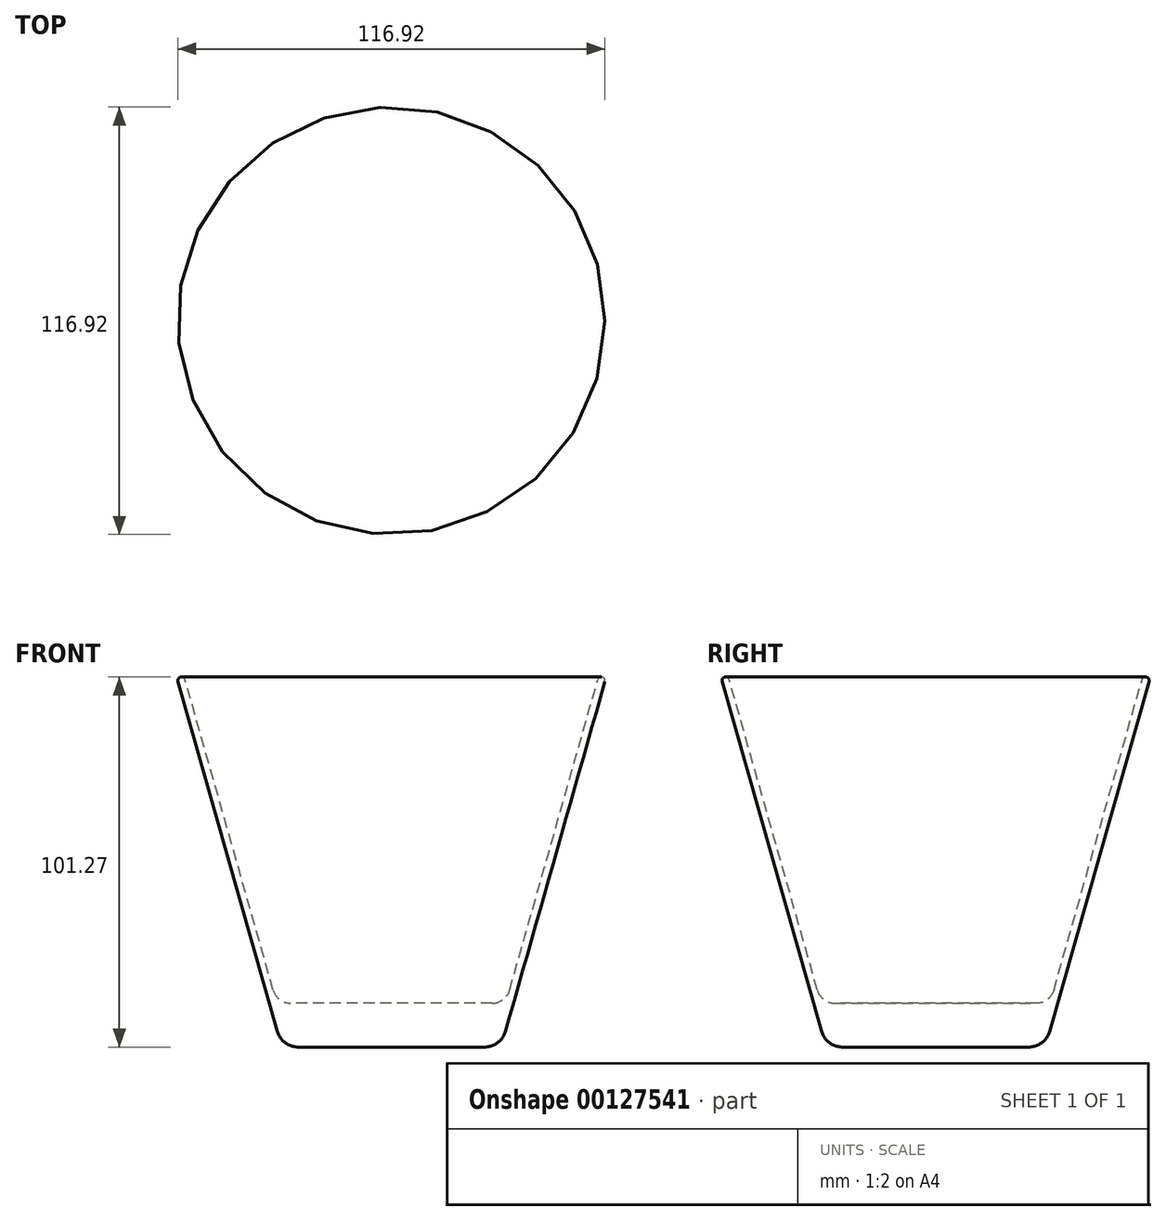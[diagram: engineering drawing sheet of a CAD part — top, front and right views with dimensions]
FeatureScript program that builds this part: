
annotation { "Feature Type Name" : "Feature", "Feature Type Description" : "" }
export const myFeature = defineFeature(function(context is Context, id is Id, definition is map)
    precondition{}
    {
        {
            var Q0;
            Q0=qCreatedBy(makeId("Front.planeOp"),FACE);
            var sketch = newSketch(context, id + "F0", { "sketchPlane" : qUnion([Q0])});
            skLineSegment(sketch, "E0", {"start": v(0, 0) * mm, "end": v(25.47, 0) * mm});
            skLineSegment(sketch, "E1", {"start": v(31.24, 4.36) * mm, "end": v(58.42, 100) * mm});
            skPoint(sketch, "E2.visualSharp", {"position": v(30, 0) * mm});
            skLineSegment(sketch, "E3.0", {"start": v(32.36, 15.63) * mm, "end": v(56.5, 100.55) * mm});
            skPoint(sketch, "E4.visualSharp", {"position": v(28.49, 2) * mm});
            skArc(sketch, "E5", {"start": v(58.42, 100) * mm, "mid": v(57.73, 101.24) * mm, "end": v(56.5, 100.55) * mm});
            skLineSegment(sketch, "E6.0", {"start": v(0, 12) * mm, "end": v(27.55, 12) * mm});
            skPoint(sketch, "E7.visualSharp", {"position": v(31.33, 12) * mm});
            skArc(sketch, "E7.filletArc", {"start": v(27.55, 12) * mm, "mid": v(30.57, 13.01) * mm, "end": v(32.36, 15.63) * mm});
            skArc(sketch, "E8.filletArc", {"start": v(25.47, 0) * mm, "mid": v(29.08, 1.21) * mm, "end": v(31.24, 4.36) * mm});
            skPoint(sketch, "E9.orphan", {"position": v(0, 100) * mm});
            skLineSegment(sketch, "E10", {"start": v(0, 12) * mm, "end": v(0, 0) * mm});
            skSolve(sketch);
        }
        {
            var Q0;
            Q0=makeQuery(id+"F0.imprint","IMPRINT",FACE,{"disambiguationData":[TD([[makeQuery(id+"F0.imprint","IMPRINT",EDGE,{"derivedFrom":sQuery(id+"F0.wireOp",EDGE,"E0")}),1.0]])]});
            var Q1;
            Q1=sQuery(id+"F0.wireOp",EDGE,"E10");
            revolve(context, id + "F1", {"entities" : qUnion([Q0]), "axis" : qUnion([Q1]), "revolveType" : RevolveType.FULL});
        }
    });
